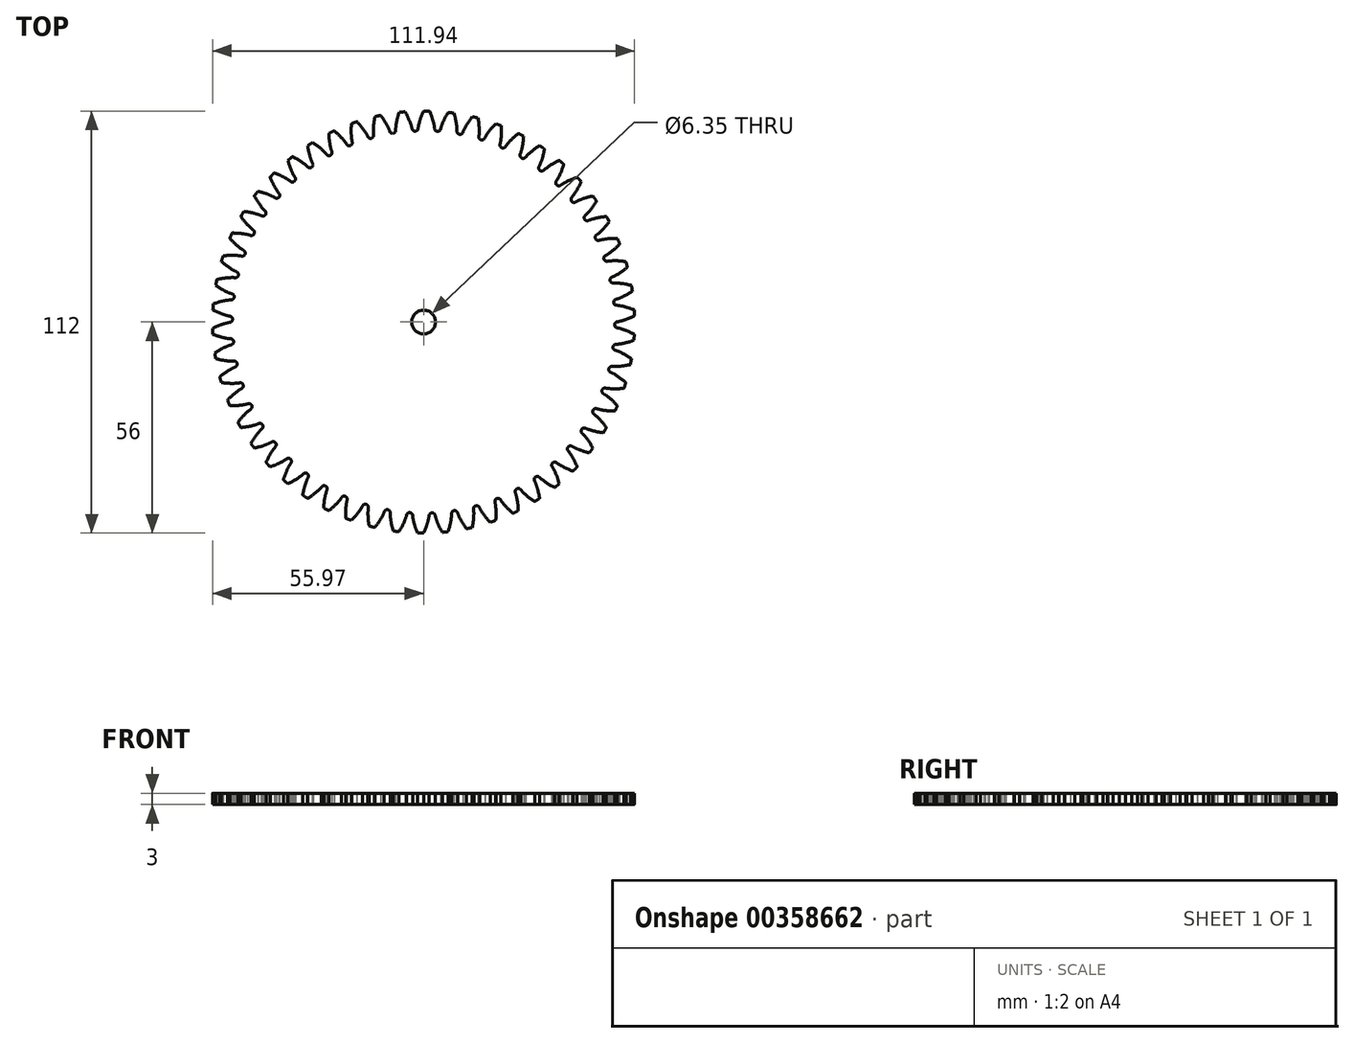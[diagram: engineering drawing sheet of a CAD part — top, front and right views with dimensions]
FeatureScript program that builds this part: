
annotation { "Feature Type Name" : "Feature", "Feature Type Description" : "" }
export const myFeature = defineFeature(function(context is Context, id is Id, definition is map)
    precondition{}
    {
        {
            assignVariable(context, id + "F0", {"name" : "T", "anyValue" : 54});
        }
        {
            var Q0;
            Q0=qCreatedBy(makeId("Top.planeOp"),FACE);
            var sketch = newSketch(context, id + "F1", { "sketchPlane" : qUnion([Q0])});
            skCircle(sketch, "E0", {"center": v(0, 0) * mm, "radius": 56 * mm});
            skCircle(sketch, "E1", {"center": v(0, 0) * mm, "radius": 54 * mm, "construction": true});
            skCircle(sketch, "E2", {"center": v(0, 0) * mm, "radius": 50.74 * mm, "construction": true});
            skCircle(sketch, "E3", {"center": v(0, 0) * mm, "radius": 51.5 * mm});
            skLineSegment(sketch, "E4", {"start": v(0, 0) * mm, "end": v(50.74, 0) * mm});
            skFitSpline(sketch, "E5", {"points": [v(50.74, 0) * mm, v(50.89, 0) * mm, v(51.3, 0.06) * mm, v(52, 0.2) * mm, v(52.97, 0.45) * mm, v(54.17, 0.87) * mm, v(55.6, 1.5) * mm, v(57.23, 2.36) * mm, v(59.03, 3.5) * mm, v(60.98, 4.93) * mm, v(63.02, 6.7) * mm], "startDerivative": vector(12.72, 0.63) * mm, "endDerivative": vector(42.04, 36.24) * mm});
            skLineSegment(sketch, "E6", {"start": v(0, 0) * mm, "end": v(56, -0.8) * mm, "construction": true});
            skLineSegment(sketch, "E7", {"start": v(0, 0) * mm, "end": v(54, 0.8) * mm, "construction": true});
            skFitSpline(sketch, "E8.MirrorCS", {"points": [v(50.72, -1.44) * mm, v(50.86, -1.45) * mm, v(51.29, -1.51) * mm, v(51.98, -1.67) * mm, v(52.93, -1.95) * mm, v(54.12, -2.4) * mm, v(55.54, -3.08) * mm, v(57.14, -3.99) * mm, v(58.91, -5.17) * mm, v(60.81, -6.66) * mm, v(62.8, -8.48) * mm], "startDerivative": vector(12.7, -1) * mm, "endDerivative": vector(41, -37.42) * mm});
            skLineSegment(sketch, "E9", {"start": v(0, 0) * mm, "end": v(50.72, -1.44) * mm});
            skSolve(sketch);
        }
        {
            var Q0;
            Q0=qCreatedBy(makeId("Top.planeOp"),FACE);
            var sketch = newSketch(context, id + "F2", { "sketchPlane" : qUnion([Q0])});
            skCircle(sketch, "E10", {"center": v(0, 0) * mm, "radius": 56 * mm});
            skSolve(sketch);
        }
        {
            var Q0;
            {var subQ0=sQuery(id+"F1.wireOp",EDGE,"E5");var subQ7=sQuery(id+"F1.wireOp",EDGE,"E0");var subQ8=makeQuery(id+"F1.imprint","INTERSECT",VERTEX,{"derivedFrom":[subQ7,subQ0]});Q0=makeQuery(id+"F1.imprint","IMPRINT",FACE,{"disambiguationData":[TD([[makeQuery(id+"F1.imprint","IMPRINT",EDGE,{"disambiguationData":[TD([[subQ8,1.0]])],"derivedFrom":subQ7}),1.0]])]});}
            extrude(context, id + "F3", {"entities" : qUnion([Q0]), "depth" : 6 * mm});
        }
        {
            var Q0;
            Q0=makeQuery(id+"F3.opExtrude","CAP_FACE",FACE,{"disambiguationData":[OSD([sQuery(id+"F1.wireOp",EDGE,"E0"),sQuery(id+"F1.wireOp",EDGE,"E3"),sQuery(id+"F1.wireOp",EDGE,"E4"),sQuery(id+"F1.wireOp",EDGE,"E5"),sQuery(id+"F1.wireOp",EDGE,"E8.MirrorCS"),sQuery(id+"F1.wireOp",EDGE,"E9")])],"isStart":true});
            var sketch = newSketch(context, id + "F4", { "sketchPlane" : qUnion([Q0])});
            skCircle(sketch, "E11", {"center": v(51.5, 0.73) * mm, "radius": 0.82 * mm});
            skSolve(sketch);
        }
        {
            var Q0;
            {var subQ1=makeQuery(id+"F3.opExtrude","CAP_EDGE",EDGE,{"disambiguationData":[OSD([sQuery(id+"F1.wireOp",EDGE,"E3")])],"isStart":true});Q0=makeQuery(id+"F4.imprint","IMPRINT",FACE,{"disambiguationData":[TD([[makeQuery(id+"F4.imprint","IMPRINT",EDGE,{"derivedFrom":subQ1}),-1.0]])]});}
            extrude(context, id + "F5", {"entities" : qUnion([Q0]), "operationType" : NewBodyOperationType.ADD, "oppositeDirection" : true, "depth" : 6 * mm});
        }
        {
            var Q0;
            Q0=makeQuery(id+"F2.imprint","IMPRINT",FACE,{"disambiguationData":[TD([[makeQuery(id+"F2.imprint","IMPRINT",EDGE,{"derivedFrom":sQuery(id+"F2.wireOp",EDGE,"E10")}),1.0]])]});
            extrude(context, id + "F6", {"entities" : qUnion([Q0]), "depth" : 3 * mm, "offsetDistance" : 25 * mm});
        }
        {
            var Q0;
            Q0=makeQuery(id+"F3.opExtrude","SWEPT_BODY",BODY,{"disambiguationData":[OSD([sQuery(id+"F1.wireOp",EDGE,"E0"),sQuery(id+"F1.wireOp",EDGE,"E3"),sQuery(id+"F1.wireOp",EDGE,"E4"),sQuery(id+"F1.wireOp",EDGE,"E5"),sQuery(id+"F1.wireOp",EDGE,"E8.MirrorCS"),sQuery(id+"F1.wireOp",EDGE,"E9")])]});
            var Q1;
            Q1=makeQuery(id+"F6.opExtrude","CAP_EDGE",EDGE,{"disambiguationData":[OSD([sQuery(id+"F2.wireOp",EDGE,"E10")])],"isStart":false});
            circularPattern(context, id + "F7", {"entities" : qUnion([Q0]), "axis" : qUnion([Q1]), "angle" : 360 * degree, "instanceCount" : getVariable(context, 'T'), "equalSpace" : true});
        }
        {
            var Q0;
            Q0=makeQuery(id+"F7.opPattern","COPY",BODY,{"derivedFrom":makeQuery(id+"F3.opExtrude","SWEPT_BODY",BODY,{"disambiguationData":[OSD([sQuery(id+"F1.wireOp",EDGE,"E0"),sQuery(id+"F1.wireOp",EDGE,"E3"),sQuery(id+"F1.wireOp",EDGE,"E4"),sQuery(id+"F1.wireOp",EDGE,"E5"),sQuery(id+"F1.wireOp",EDGE,"E8.MirrorCS"),sQuery(id+"F1.wireOp",EDGE,"E9")])]}),"instanceName":"5"});
            var Q1;
            Q1=makeQuery(id+"F7.opPattern","COPY",BODY,{"derivedFrom":makeQuery(id+"F3.opExtrude","SWEPT_BODY",BODY,{"disambiguationData":[OSD([sQuery(id+"F1.wireOp",EDGE,"E0"),sQuery(id+"F1.wireOp",EDGE,"E3"),sQuery(id+"F1.wireOp",EDGE,"E4"),sQuery(id+"F1.wireOp",EDGE,"E5"),sQuery(id+"F1.wireOp",EDGE,"E8.MirrorCS"),sQuery(id+"F1.wireOp",EDGE,"E9")])]}),"instanceName":"6"});
            var Q2;
            Q2=makeQuery(id+"F7.opPattern","COPY",BODY,{"derivedFrom":makeQuery(id+"F3.opExtrude","SWEPT_BODY",BODY,{"disambiguationData":[OSD([sQuery(id+"F1.wireOp",EDGE,"E0"),sQuery(id+"F1.wireOp",EDGE,"E3"),sQuery(id+"F1.wireOp",EDGE,"E4"),sQuery(id+"F1.wireOp",EDGE,"E5"),sQuery(id+"F1.wireOp",EDGE,"E8.MirrorCS"),sQuery(id+"F1.wireOp",EDGE,"E9")])]}),"instanceName":"7"});
            var Q3;
            Q3=makeQuery(id+"F7.opPattern","COPY",BODY,{"derivedFrom":makeQuery(id+"F3.opExtrude","SWEPT_BODY",BODY,{"disambiguationData":[OSD([sQuery(id+"F1.wireOp",EDGE,"E0"),sQuery(id+"F1.wireOp",EDGE,"E3"),sQuery(id+"F1.wireOp",EDGE,"E4"),sQuery(id+"F1.wireOp",EDGE,"E5"),sQuery(id+"F1.wireOp",EDGE,"E8.MirrorCS"),sQuery(id+"F1.wireOp",EDGE,"E9")])]}),"instanceName":"8"});
            var Q4;
            Q4=makeQuery(id+"F7.opPattern","COPY",BODY,{"derivedFrom":makeQuery(id+"F3.opExtrude","SWEPT_BODY",BODY,{"disambiguationData":[OSD([sQuery(id+"F1.wireOp",EDGE,"E0"),sQuery(id+"F1.wireOp",EDGE,"E3"),sQuery(id+"F1.wireOp",EDGE,"E4"),sQuery(id+"F1.wireOp",EDGE,"E5"),sQuery(id+"F1.wireOp",EDGE,"E8.MirrorCS"),sQuery(id+"F1.wireOp",EDGE,"E9")])]}),"instanceName":"9"});
            var Q5;
            Q5=makeQuery(id+"F7.opPattern","COPY",BODY,{"derivedFrom":makeQuery(id+"F3.opExtrude","SWEPT_BODY",BODY,{"disambiguationData":[OSD([sQuery(id+"F1.wireOp",EDGE,"E0"),sQuery(id+"F1.wireOp",EDGE,"E3"),sQuery(id+"F1.wireOp",EDGE,"E4"),sQuery(id+"F1.wireOp",EDGE,"E5"),sQuery(id+"F1.wireOp",EDGE,"E8.MirrorCS"),sQuery(id+"F1.wireOp",EDGE,"E9")])]}),"instanceName":"10"});
            var Q6;
            Q6=makeQuery(id+"F7.opPattern","COPY",BODY,{"derivedFrom":makeQuery(id+"F3.opExtrude","SWEPT_BODY",BODY,{"disambiguationData":[OSD([sQuery(id+"F1.wireOp",EDGE,"E0"),sQuery(id+"F1.wireOp",EDGE,"E3"),sQuery(id+"F1.wireOp",EDGE,"E4"),sQuery(id+"F1.wireOp",EDGE,"E5"),sQuery(id+"F1.wireOp",EDGE,"E8.MirrorCS"),sQuery(id+"F1.wireOp",EDGE,"E9")])]}),"instanceName":"11"});
            var Q7;
            Q7=makeQuery(id+"F7.opPattern","COPY",BODY,{"derivedFrom":makeQuery(id+"F3.opExtrude","SWEPT_BODY",BODY,{"disambiguationData":[OSD([sQuery(id+"F1.wireOp",EDGE,"E0"),sQuery(id+"F1.wireOp",EDGE,"E3"),sQuery(id+"F1.wireOp",EDGE,"E4"),sQuery(id+"F1.wireOp",EDGE,"E5"),sQuery(id+"F1.wireOp",EDGE,"E8.MirrorCS"),sQuery(id+"F1.wireOp",EDGE,"E9")])]}),"instanceName":"12"});
            var Q8;
            Q8=makeQuery(id+"F7.opPattern","COPY",BODY,{"derivedFrom":makeQuery(id+"F3.opExtrude","SWEPT_BODY",BODY,{"disambiguationData":[OSD([sQuery(id+"F1.wireOp",EDGE,"E0"),sQuery(id+"F1.wireOp",EDGE,"E3"),sQuery(id+"F1.wireOp",EDGE,"E4"),sQuery(id+"F1.wireOp",EDGE,"E5"),sQuery(id+"F1.wireOp",EDGE,"E8.MirrorCS"),sQuery(id+"F1.wireOp",EDGE,"E9")])]}),"instanceName":"13"});
            var Q9;
            Q9=makeQuery(id+"F7.opPattern","COPY",BODY,{"derivedFrom":makeQuery(id+"F3.opExtrude","SWEPT_BODY",BODY,{"disambiguationData":[OSD([sQuery(id+"F1.wireOp",EDGE,"E0"),sQuery(id+"F1.wireOp",EDGE,"E3"),sQuery(id+"F1.wireOp",EDGE,"E4"),sQuery(id+"F1.wireOp",EDGE,"E5"),sQuery(id+"F1.wireOp",EDGE,"E8.MirrorCS"),sQuery(id+"F1.wireOp",EDGE,"E9")])]}),"instanceName":"14"});
            var Q10;
            Q10=makeQuery(id+"F7.opPattern","COPY",BODY,{"derivedFrom":makeQuery(id+"F3.opExtrude","SWEPT_BODY",BODY,{"disambiguationData":[OSD([sQuery(id+"F1.wireOp",EDGE,"E0"),sQuery(id+"F1.wireOp",EDGE,"E3"),sQuery(id+"F1.wireOp",EDGE,"E4"),sQuery(id+"F1.wireOp",EDGE,"E5"),sQuery(id+"F1.wireOp",EDGE,"E8.MirrorCS"),sQuery(id+"F1.wireOp",EDGE,"E9")])]}),"instanceName":"15"});
            var Q11;
            Q11=makeQuery(id+"F7.opPattern","COPY",BODY,{"derivedFrom":makeQuery(id+"F3.opExtrude","SWEPT_BODY",BODY,{"disambiguationData":[OSD([sQuery(id+"F1.wireOp",EDGE,"E0"),sQuery(id+"F1.wireOp",EDGE,"E3"),sQuery(id+"F1.wireOp",EDGE,"E4"),sQuery(id+"F1.wireOp",EDGE,"E5"),sQuery(id+"F1.wireOp",EDGE,"E8.MirrorCS"),sQuery(id+"F1.wireOp",EDGE,"E9")])]}),"instanceName":"16"});
            var Q12;
            Q12=makeQuery(id+"F7.opPattern","COPY",BODY,{"derivedFrom":makeQuery(id+"F3.opExtrude","SWEPT_BODY",BODY,{"disambiguationData":[OSD([sQuery(id+"F1.wireOp",EDGE,"E0"),sQuery(id+"F1.wireOp",EDGE,"E3"),sQuery(id+"F1.wireOp",EDGE,"E4"),sQuery(id+"F1.wireOp",EDGE,"E5"),sQuery(id+"F1.wireOp",EDGE,"E8.MirrorCS"),sQuery(id+"F1.wireOp",EDGE,"E9")])]}),"instanceName":"17"});
            var Q13;
            Q13=makeQuery(id+"F7.opPattern","COPY",BODY,{"derivedFrom":makeQuery(id+"F3.opExtrude","SWEPT_BODY",BODY,{"disambiguationData":[OSD([sQuery(id+"F1.wireOp",EDGE,"E0"),sQuery(id+"F1.wireOp",EDGE,"E3"),sQuery(id+"F1.wireOp",EDGE,"E4"),sQuery(id+"F1.wireOp",EDGE,"E5"),sQuery(id+"F1.wireOp",EDGE,"E8.MirrorCS"),sQuery(id+"F1.wireOp",EDGE,"E9")])]}),"instanceName":"18"});
            var Q14;
            Q14=makeQuery(id+"F7.opPattern","COPY",BODY,{"derivedFrom":makeQuery(id+"F3.opExtrude","SWEPT_BODY",BODY,{"disambiguationData":[OSD([sQuery(id+"F1.wireOp",EDGE,"E0"),sQuery(id+"F1.wireOp",EDGE,"E3"),sQuery(id+"F1.wireOp",EDGE,"E4"),sQuery(id+"F1.wireOp",EDGE,"E5"),sQuery(id+"F1.wireOp",EDGE,"E8.MirrorCS"),sQuery(id+"F1.wireOp",EDGE,"E9")])]}),"instanceName":"19"});
            var Q15;
            Q15=makeQuery(id+"F7.opPattern","COPY",BODY,{"derivedFrom":makeQuery(id+"F3.opExtrude","SWEPT_BODY",BODY,{"disambiguationData":[OSD([sQuery(id+"F1.wireOp",EDGE,"E0"),sQuery(id+"F1.wireOp",EDGE,"E3"),sQuery(id+"F1.wireOp",EDGE,"E4"),sQuery(id+"F1.wireOp",EDGE,"E5"),sQuery(id+"F1.wireOp",EDGE,"E8.MirrorCS"),sQuery(id+"F1.wireOp",EDGE,"E9")])]}),"instanceName":"20"});
            var Q16;
            Q16=makeQuery(id+"F7.opPattern","COPY",BODY,{"derivedFrom":makeQuery(id+"F3.opExtrude","SWEPT_BODY",BODY,{"disambiguationData":[OSD([sQuery(id+"F1.wireOp",EDGE,"E0"),sQuery(id+"F1.wireOp",EDGE,"E3"),sQuery(id+"F1.wireOp",EDGE,"E4"),sQuery(id+"F1.wireOp",EDGE,"E5"),sQuery(id+"F1.wireOp",EDGE,"E8.MirrorCS"),sQuery(id+"F1.wireOp",EDGE,"E9")])]}),"instanceName":"21"});
            var Q17;
            Q17=makeQuery(id+"F7.opPattern","COPY",BODY,{"derivedFrom":makeQuery(id+"F3.opExtrude","SWEPT_BODY",BODY,{"disambiguationData":[OSD([sQuery(id+"F1.wireOp",EDGE,"E0"),sQuery(id+"F1.wireOp",EDGE,"E3"),sQuery(id+"F1.wireOp",EDGE,"E4"),sQuery(id+"F1.wireOp",EDGE,"E5"),sQuery(id+"F1.wireOp",EDGE,"E8.MirrorCS"),sQuery(id+"F1.wireOp",EDGE,"E9")])]}),"instanceName":"22"});
            var Q18;
            Q18=makeQuery(id+"F7.opPattern","COPY",BODY,{"derivedFrom":makeQuery(id+"F3.opExtrude","SWEPT_BODY",BODY,{"disambiguationData":[OSD([sQuery(id+"F1.wireOp",EDGE,"E0"),sQuery(id+"F1.wireOp",EDGE,"E3"),sQuery(id+"F1.wireOp",EDGE,"E4"),sQuery(id+"F1.wireOp",EDGE,"E5"),sQuery(id+"F1.wireOp",EDGE,"E8.MirrorCS"),sQuery(id+"F1.wireOp",EDGE,"E9")])]}),"instanceName":"23"});
            var Q19;
            Q19=makeQuery(id+"F7.opPattern","COPY",BODY,{"derivedFrom":makeQuery(id+"F3.opExtrude","SWEPT_BODY",BODY,{"disambiguationData":[OSD([sQuery(id+"F1.wireOp",EDGE,"E0"),sQuery(id+"F1.wireOp",EDGE,"E3"),sQuery(id+"F1.wireOp",EDGE,"E4"),sQuery(id+"F1.wireOp",EDGE,"E5"),sQuery(id+"F1.wireOp",EDGE,"E8.MirrorCS"),sQuery(id+"F1.wireOp",EDGE,"E9")])]}),"instanceName":"24"});
            var Q20;
            Q20=makeQuery(id+"F7.opPattern","COPY",BODY,{"derivedFrom":makeQuery(id+"F3.opExtrude","SWEPT_BODY",BODY,{"disambiguationData":[OSD([sQuery(id+"F1.wireOp",EDGE,"E0"),sQuery(id+"F1.wireOp",EDGE,"E3"),sQuery(id+"F1.wireOp",EDGE,"E4"),sQuery(id+"F1.wireOp",EDGE,"E5"),sQuery(id+"F1.wireOp",EDGE,"E8.MirrorCS"),sQuery(id+"F1.wireOp",EDGE,"E9")])]}),"instanceName":"25"});
            var Q21;
            Q21=makeQuery(id+"F7.opPattern","COPY",BODY,{"derivedFrom":makeQuery(id+"F3.opExtrude","SWEPT_BODY",BODY,{"disambiguationData":[OSD([sQuery(id+"F1.wireOp",EDGE,"E0"),sQuery(id+"F1.wireOp",EDGE,"E3"),sQuery(id+"F1.wireOp",EDGE,"E4"),sQuery(id+"F1.wireOp",EDGE,"E5"),sQuery(id+"F1.wireOp",EDGE,"E8.MirrorCS"),sQuery(id+"F1.wireOp",EDGE,"E9")])]}),"instanceName":"26"});
            var Q22;
            Q22=makeQuery(id+"F7.opPattern","COPY",BODY,{"derivedFrom":makeQuery(id+"F3.opExtrude","SWEPT_BODY",BODY,{"disambiguationData":[OSD([sQuery(id+"F1.wireOp",EDGE,"E0"),sQuery(id+"F1.wireOp",EDGE,"E3"),sQuery(id+"F1.wireOp",EDGE,"E4"),sQuery(id+"F1.wireOp",EDGE,"E5"),sQuery(id+"F1.wireOp",EDGE,"E8.MirrorCS"),sQuery(id+"F1.wireOp",EDGE,"E9")])]}),"instanceName":"27"});
            var Q23;
            Q23=makeQuery(id+"F7.opPattern","COPY",BODY,{"derivedFrom":makeQuery(id+"F3.opExtrude","SWEPT_BODY",BODY,{"disambiguationData":[OSD([sQuery(id+"F1.wireOp",EDGE,"E0"),sQuery(id+"F1.wireOp",EDGE,"E3"),sQuery(id+"F1.wireOp",EDGE,"E4"),sQuery(id+"F1.wireOp",EDGE,"E5"),sQuery(id+"F1.wireOp",EDGE,"E8.MirrorCS"),sQuery(id+"F1.wireOp",EDGE,"E9")])]}),"instanceName":"28"});
            var Q24;
            Q24=makeQuery(id+"F7.opPattern","COPY",BODY,{"derivedFrom":makeQuery(id+"F3.opExtrude","SWEPT_BODY",BODY,{"disambiguationData":[OSD([sQuery(id+"F1.wireOp",EDGE,"E0"),sQuery(id+"F1.wireOp",EDGE,"E3"),sQuery(id+"F1.wireOp",EDGE,"E4"),sQuery(id+"F1.wireOp",EDGE,"E5"),sQuery(id+"F1.wireOp",EDGE,"E8.MirrorCS"),sQuery(id+"F1.wireOp",EDGE,"E9")])]}),"instanceName":"29"});
            var Q25;
            Q25=makeQuery(id+"F3.opExtrude","SWEPT_BODY",BODY,{"disambiguationData":[OSD([sQuery(id+"F1.wireOp",EDGE,"E0"),sQuery(id+"F1.wireOp",EDGE,"E3"),sQuery(id+"F1.wireOp",EDGE,"E4"),sQuery(id+"F1.wireOp",EDGE,"E5"),sQuery(id+"F1.wireOp",EDGE,"E8.MirrorCS"),sQuery(id+"F1.wireOp",EDGE,"E9")])]});
            var Q26;
            Q26=makeQuery(id+"F7.opPattern","COPY",BODY,{"derivedFrom":makeQuery(id+"F3.opExtrude","SWEPT_BODY",BODY,{"disambiguationData":[OSD([sQuery(id+"F1.wireOp",EDGE,"E0"),sQuery(id+"F1.wireOp",EDGE,"E3"),sQuery(id+"F1.wireOp",EDGE,"E4"),sQuery(id+"F1.wireOp",EDGE,"E5"),sQuery(id+"F1.wireOp",EDGE,"E8.MirrorCS"),sQuery(id+"F1.wireOp",EDGE,"E9")])]}),"instanceName":"1"});
            var Q27;
            Q27=makeQuery(id+"F7.opPattern","COPY",BODY,{"derivedFrom":makeQuery(id+"F3.opExtrude","SWEPT_BODY",BODY,{"disambiguationData":[OSD([sQuery(id+"F1.wireOp",EDGE,"E0"),sQuery(id+"F1.wireOp",EDGE,"E3"),sQuery(id+"F1.wireOp",EDGE,"E4"),sQuery(id+"F1.wireOp",EDGE,"E5"),sQuery(id+"F1.wireOp",EDGE,"E8.MirrorCS"),sQuery(id+"F1.wireOp",EDGE,"E9")])]}),"instanceName":"2"});
            var Q28;
            Q28=makeQuery(id+"F7.opPattern","COPY",BODY,{"derivedFrom":makeQuery(id+"F3.opExtrude","SWEPT_BODY",BODY,{"disambiguationData":[OSD([sQuery(id+"F1.wireOp",EDGE,"E0"),sQuery(id+"F1.wireOp",EDGE,"E3"),sQuery(id+"F1.wireOp",EDGE,"E4"),sQuery(id+"F1.wireOp",EDGE,"E5"),sQuery(id+"F1.wireOp",EDGE,"E8.MirrorCS"),sQuery(id+"F1.wireOp",EDGE,"E9")])]}),"instanceName":"3"});
            var Q29;
            Q29=makeQuery(id+"F7.opPattern","COPY",BODY,{"derivedFrom":makeQuery(id+"F3.opExtrude","SWEPT_BODY",BODY,{"disambiguationData":[OSD([sQuery(id+"F1.wireOp",EDGE,"E0"),sQuery(id+"F1.wireOp",EDGE,"E3"),sQuery(id+"F1.wireOp",EDGE,"E4"),sQuery(id+"F1.wireOp",EDGE,"E5"),sQuery(id+"F1.wireOp",EDGE,"E8.MirrorCS"),sQuery(id+"F1.wireOp",EDGE,"E9")])]}),"instanceName":"4"});
            var Q30;
            Q30=makeQuery(id+"F7.opPattern","COPY",BODY,{"derivedFrom":makeQuery(id+"F3.opExtrude","SWEPT_BODY",BODY,{"disambiguationData":[OSD([sQuery(id+"F1.wireOp",EDGE,"E0"),sQuery(id+"F1.wireOp",EDGE,"E3"),sQuery(id+"F1.wireOp",EDGE,"E5"),sQuery(id+"F1.wireOp",EDGE,"E8.MirrorCS")])]}),"instanceName":"30"});
            var Q31;
            Q31=makeQuery(id+"F7.opPattern","COPY",BODY,{"derivedFrom":makeQuery(id+"F3.opExtrude","SWEPT_BODY",BODY,{"disambiguationData":[OSD([sQuery(id+"F1.wireOp",EDGE,"E0"),sQuery(id+"F1.wireOp",EDGE,"E3"),sQuery(id+"F1.wireOp",EDGE,"E5"),sQuery(id+"F1.wireOp",EDGE,"E8.MirrorCS")])]}),"instanceName":"31"});
            var Q32;
            Q32=makeQuery(id+"F7.opPattern","COPY",BODY,{"derivedFrom":makeQuery(id+"F3.opExtrude","SWEPT_BODY",BODY,{"disambiguationData":[OSD([sQuery(id+"F1.wireOp",EDGE,"E0"),sQuery(id+"F1.wireOp",EDGE,"E3"),sQuery(id+"F1.wireOp",EDGE,"E5"),sQuery(id+"F1.wireOp",EDGE,"E8.MirrorCS")])]}),"instanceName":"32"});
            var Q33;
            Q33=makeQuery(id+"F7.opPattern","COPY",BODY,{"derivedFrom":makeQuery(id+"F3.opExtrude","SWEPT_BODY",BODY,{"disambiguationData":[OSD([sQuery(id+"F1.wireOp",EDGE,"E0"),sQuery(id+"F1.wireOp",EDGE,"E3"),sQuery(id+"F1.wireOp",EDGE,"E5"),sQuery(id+"F1.wireOp",EDGE,"E8.MirrorCS")])]}),"instanceName":"33"});
            var Q34;
            Q34=makeQuery(id+"F7.opPattern","COPY",BODY,{"derivedFrom":makeQuery(id+"F3.opExtrude","SWEPT_BODY",BODY,{"disambiguationData":[OSD([sQuery(id+"F1.wireOp",EDGE,"E0"),sQuery(id+"F1.wireOp",EDGE,"E3"),sQuery(id+"F1.wireOp",EDGE,"E5"),sQuery(id+"F1.wireOp",EDGE,"E8.MirrorCS")])]}),"instanceName":"34"});
            var Q35;
            Q35=makeQuery(id+"F7.opPattern","COPY",BODY,{"derivedFrom":makeQuery(id+"F3.opExtrude","SWEPT_BODY",BODY,{"disambiguationData":[OSD([sQuery(id+"F1.wireOp",EDGE,"E0"),sQuery(id+"F1.wireOp",EDGE,"E3"),sQuery(id+"F1.wireOp",EDGE,"E5"),sQuery(id+"F1.wireOp",EDGE,"E8.MirrorCS")])]}),"instanceName":"35"});
            var Q36;
            Q36=makeQuery(id+"F7.opPattern","COPY",BODY,{"derivedFrom":makeQuery(id+"F3.opExtrude","SWEPT_BODY",BODY,{"disambiguationData":[OSD([sQuery(id+"F1.wireOp",EDGE,"E0"),sQuery(id+"F1.wireOp",EDGE,"E3"),sQuery(id+"F1.wireOp",EDGE,"E5"),sQuery(id+"F1.wireOp",EDGE,"E8.MirrorCS")])]}),"instanceName":"36"});
            var Q37;
            Q37=makeQuery(id+"F7.opPattern","COPY",BODY,{"derivedFrom":makeQuery(id+"F3.opExtrude","SWEPT_BODY",BODY,{"disambiguationData":[OSD([sQuery(id+"F1.wireOp",EDGE,"E0"),sQuery(id+"F1.wireOp",EDGE,"E3"),sQuery(id+"F1.wireOp",EDGE,"E5"),sQuery(id+"F1.wireOp",EDGE,"E8.MirrorCS")])]}),"instanceName":"37"});
            var Q38;
            Q38=makeQuery(id+"F7.opPattern","COPY",BODY,{"derivedFrom":makeQuery(id+"F3.opExtrude","SWEPT_BODY",BODY,{"disambiguationData":[OSD([sQuery(id+"F1.wireOp",EDGE,"E0"),sQuery(id+"F1.wireOp",EDGE,"E3"),sQuery(id+"F1.wireOp",EDGE,"E5"),sQuery(id+"F1.wireOp",EDGE,"E8.MirrorCS")])]}),"instanceName":"38"});
            var Q39;
            Q39=makeQuery(id+"F7.opPattern","COPY",BODY,{"derivedFrom":makeQuery(id+"F3.opExtrude","SWEPT_BODY",BODY,{"disambiguationData":[OSD([sQuery(id+"F1.wireOp",EDGE,"E0"),sQuery(id+"F1.wireOp",EDGE,"E3"),sQuery(id+"F1.wireOp",EDGE,"E5"),sQuery(id+"F1.wireOp",EDGE,"E8.MirrorCS")])]}),"instanceName":"39"});
            var Q40;
            Q40=makeQuery(id+"F7.opPattern","COPY",BODY,{"derivedFrom":makeQuery(id+"F3.opExtrude","SWEPT_BODY",BODY,{"disambiguationData":[OSD([sQuery(id+"F1.wireOp",EDGE,"E0"),sQuery(id+"F1.wireOp",EDGE,"E3"),sQuery(id+"F1.wireOp",EDGE,"E5"),sQuery(id+"F1.wireOp",EDGE,"E8.MirrorCS")])]}),"instanceName":"40"});
            var Q41;
            Q41=makeQuery(id+"F7.opPattern","COPY",BODY,{"derivedFrom":makeQuery(id+"F3.opExtrude","SWEPT_BODY",BODY,{"disambiguationData":[OSD([sQuery(id+"F1.wireOp",EDGE,"E0"),sQuery(id+"F1.wireOp",EDGE,"E3"),sQuery(id+"F1.wireOp",EDGE,"E5"),sQuery(id+"F1.wireOp",EDGE,"E8.MirrorCS")])]}),"instanceName":"41"});
            var Q42;
            Q42=makeQuery(id+"F7.opPattern","COPY",BODY,{"derivedFrom":makeQuery(id+"F3.opExtrude","SWEPT_BODY",BODY,{"disambiguationData":[OSD([sQuery(id+"F1.wireOp",EDGE,"E0"),sQuery(id+"F1.wireOp",EDGE,"E3"),sQuery(id+"F1.wireOp",EDGE,"E5"),sQuery(id+"F1.wireOp",EDGE,"E8.MirrorCS")])]}),"instanceName":"42"});
            var Q43;
            Q43=makeQuery(id+"F7.opPattern","COPY",BODY,{"derivedFrom":makeQuery(id+"F3.opExtrude","SWEPT_BODY",BODY,{"disambiguationData":[OSD([sQuery(id+"F1.wireOp",EDGE,"E0"),sQuery(id+"F1.wireOp",EDGE,"E3"),sQuery(id+"F1.wireOp",EDGE,"E5"),sQuery(id+"F1.wireOp",EDGE,"E8.MirrorCS")])]}),"instanceName":"43"});
            var Q44;
            Q44=makeQuery(id+"F7.opPattern","COPY",BODY,{"derivedFrom":makeQuery(id+"F3.opExtrude","SWEPT_BODY",BODY,{"disambiguationData":[OSD([sQuery(id+"F1.wireOp",EDGE,"E0"),sQuery(id+"F1.wireOp",EDGE,"E3"),sQuery(id+"F1.wireOp",EDGE,"E5"),sQuery(id+"F1.wireOp",EDGE,"E8.MirrorCS")])]}),"instanceName":"44"});
            var Q45;
            Q45=makeQuery(id+"F7.opPattern","COPY",BODY,{"derivedFrom":makeQuery(id+"F3.opExtrude","SWEPT_BODY",BODY,{"disambiguationData":[OSD([sQuery(id+"F1.wireOp",EDGE,"E0"),sQuery(id+"F1.wireOp",EDGE,"E3"),sQuery(id+"F1.wireOp",EDGE,"E5"),sQuery(id+"F1.wireOp",EDGE,"E8.MirrorCS")])]}),"instanceName":"45"});
            var Q46;
            Q46=makeQuery(id+"F7.opPattern","COPY",BODY,{"derivedFrom":makeQuery(id+"F3.opExtrude","SWEPT_BODY",BODY,{"disambiguationData":[OSD([sQuery(id+"F1.wireOp",EDGE,"E0"),sQuery(id+"F1.wireOp",EDGE,"E3"),sQuery(id+"F1.wireOp",EDGE,"E5"),sQuery(id+"F1.wireOp",EDGE,"E8.MirrorCS")])]}),"instanceName":"46"});
            var Q47;
            Q47=makeQuery(id+"F7.opPattern","COPY",BODY,{"derivedFrom":makeQuery(id+"F3.opExtrude","SWEPT_BODY",BODY,{"disambiguationData":[OSD([sQuery(id+"F1.wireOp",EDGE,"E0"),sQuery(id+"F1.wireOp",EDGE,"E3"),sQuery(id+"F1.wireOp",EDGE,"E5"),sQuery(id+"F1.wireOp",EDGE,"E8.MirrorCS")])]}),"instanceName":"47"});
            var Q48;
            Q48=makeQuery(id+"F7.opPattern","COPY",BODY,{"derivedFrom":makeQuery(id+"F3.opExtrude","SWEPT_BODY",BODY,{"disambiguationData":[OSD([sQuery(id+"F1.wireOp",EDGE,"E0"),sQuery(id+"F1.wireOp",EDGE,"E3"),sQuery(id+"F1.wireOp",EDGE,"E5"),sQuery(id+"F1.wireOp",EDGE,"E8.MirrorCS")])]}),"instanceName":"48"});
            var Q49;
            Q49=makeQuery(id+"F7.opPattern","COPY",BODY,{"derivedFrom":makeQuery(id+"F3.opExtrude","SWEPT_BODY",BODY,{"disambiguationData":[OSD([sQuery(id+"F1.wireOp",EDGE,"E0"),sQuery(id+"F1.wireOp",EDGE,"E3"),sQuery(id+"F1.wireOp",EDGE,"E5"),sQuery(id+"F1.wireOp",EDGE,"E8.MirrorCS")])]}),"instanceName":"49"});
            var Q50;
            Q50=makeQuery(id+"F7.opPattern","COPY",BODY,{"derivedFrom":makeQuery(id+"F3.opExtrude","SWEPT_BODY",BODY,{"disambiguationData":[OSD([sQuery(id+"F1.wireOp",EDGE,"E0"),sQuery(id+"F1.wireOp",EDGE,"E3"),sQuery(id+"F1.wireOp",EDGE,"E5"),sQuery(id+"F1.wireOp",EDGE,"E8.MirrorCS")])]}),"instanceName":"50"});
            var Q51;
            Q51=makeQuery(id+"F7.opPattern","COPY",BODY,{"derivedFrom":makeQuery(id+"F3.opExtrude","SWEPT_BODY",BODY,{"disambiguationData":[OSD([sQuery(id+"F1.wireOp",EDGE,"E0"),sQuery(id+"F1.wireOp",EDGE,"E3"),sQuery(id+"F1.wireOp",EDGE,"E5"),sQuery(id+"F1.wireOp",EDGE,"E8.MirrorCS")])]}),"instanceName":"51"});
            var Q52;
            Q52=makeQuery(id+"F7.opPattern","COPY",BODY,{"derivedFrom":makeQuery(id+"F3.opExtrude","SWEPT_BODY",BODY,{"disambiguationData":[OSD([sQuery(id+"F1.wireOp",EDGE,"E0"),sQuery(id+"F1.wireOp",EDGE,"E3"),sQuery(id+"F1.wireOp",EDGE,"E5"),sQuery(id+"F1.wireOp",EDGE,"E8.MirrorCS")])]}),"instanceName":"52"});
            var Q53;
            Q53=makeQuery(id+"F7.opPattern","COPY",BODY,{"derivedFrom":makeQuery(id+"F3.opExtrude","SWEPT_BODY",BODY,{"disambiguationData":[OSD([sQuery(id+"F1.wireOp",EDGE,"E0"),sQuery(id+"F1.wireOp",EDGE,"E3"),sQuery(id+"F1.wireOp",EDGE,"E5"),sQuery(id+"F1.wireOp",EDGE,"E8.MirrorCS")])]}),"instanceName":"53"});
            var Q54;
            Q54=makeQuery(id+"F7.opPattern","COPY",BODY,{"derivedFrom":makeQuery(id+"F3.opExtrude","SWEPT_BODY",BODY,{"disambiguationData":[OSD([sQuery(id+"F1.wireOp",EDGE,"E0"),sQuery(id+"F1.wireOp",EDGE,"E3"),sQuery(id+"F1.wireOp",EDGE,"E5"),sQuery(id+"F1.wireOp",EDGE,"E8.MirrorCS")])]}),"instanceName":"54"});
            var Q55;
            Q55=makeQuery(id+"F7.opPattern","COPY",BODY,{"derivedFrom":makeQuery(id+"F3.opExtrude","SWEPT_BODY",BODY,{"disambiguationData":[OSD([sQuery(id+"F1.wireOp",EDGE,"E0"),sQuery(id+"F1.wireOp",EDGE,"E3"),sQuery(id+"F1.wireOp",EDGE,"E5"),sQuery(id+"F1.wireOp",EDGE,"E8.MirrorCS")])]}),"instanceName":"55"});
            var Q56;
            Q56=makeQuery(id+"F7.opPattern","COPY",BODY,{"derivedFrom":makeQuery(id+"F3.opExtrude","SWEPT_BODY",BODY,{"disambiguationData":[OSD([sQuery(id+"F1.wireOp",EDGE,"E0"),sQuery(id+"F1.wireOp",EDGE,"E3"),sQuery(id+"F1.wireOp",EDGE,"E5"),sQuery(id+"F1.wireOp",EDGE,"E8.MirrorCS")])]}),"instanceName":"56"});
            var Q57;
            Q57=makeQuery(id+"F7.opPattern","COPY",BODY,{"derivedFrom":makeQuery(id+"F3.opExtrude","SWEPT_BODY",BODY,{"disambiguationData":[OSD([sQuery(id+"F1.wireOp",EDGE,"E0"),sQuery(id+"F1.wireOp",EDGE,"E3"),sQuery(id+"F1.wireOp",EDGE,"E5"),sQuery(id+"F1.wireOp",EDGE,"E8.MirrorCS")])]}),"instanceName":"57"});
            var Q58;
            Q58=makeQuery(id+"F7.opPattern","COPY",BODY,{"derivedFrom":makeQuery(id+"F3.opExtrude","SWEPT_BODY",BODY,{"disambiguationData":[OSD([sQuery(id+"F1.wireOp",EDGE,"E0"),sQuery(id+"F1.wireOp",EDGE,"E3"),sQuery(id+"F1.wireOp",EDGE,"E5"),sQuery(id+"F1.wireOp",EDGE,"E8.MirrorCS")])]}),"instanceName":"58"});
            var Q59;
            Q59=makeQuery(id+"F7.opPattern","COPY",BODY,{"derivedFrom":makeQuery(id+"F3.opExtrude","SWEPT_BODY",BODY,{"disambiguationData":[OSD([sQuery(id+"F1.wireOp",EDGE,"E0"),sQuery(id+"F1.wireOp",EDGE,"E3"),sQuery(id+"F1.wireOp",EDGE,"E5"),sQuery(id+"F1.wireOp",EDGE,"E8.MirrorCS")])]}),"instanceName":"59"});
            var Q60;
            Q60=makeQuery(id+"F7.opPattern","COPY",BODY,{"derivedFrom":makeQuery(id+"F3.opExtrude","SWEPT_BODY",BODY,{"disambiguationData":[OSD([sQuery(id+"F1.wireOp",EDGE,"E0"),sQuery(id+"F1.wireOp",EDGE,"E3"),sQuery(id+"F1.wireOp",EDGE,"E5"),sQuery(id+"F1.wireOp",EDGE,"E8.MirrorCS")])]}),"instanceName":"60"});
            var Q61;
            Q61=makeQuery(id+"F7.opPattern","COPY",BODY,{"derivedFrom":makeQuery(id+"F3.opExtrude","SWEPT_BODY",BODY,{"disambiguationData":[OSD([sQuery(id+"F1.wireOp",EDGE,"E0"),sQuery(id+"F1.wireOp",EDGE,"E3"),sQuery(id+"F1.wireOp",EDGE,"E5"),sQuery(id+"F1.wireOp",EDGE,"E8.MirrorCS")])]}),"instanceName":"61"});
            var Q62;
            Q62=makeQuery(id+"F7.opPattern","COPY",BODY,{"derivedFrom":makeQuery(id+"F3.opExtrude","SWEPT_BODY",BODY,{"disambiguationData":[OSD([sQuery(id+"F1.wireOp",EDGE,"E0"),sQuery(id+"F1.wireOp",EDGE,"E3"),sQuery(id+"F1.wireOp",EDGE,"E5"),sQuery(id+"F1.wireOp",EDGE,"E8.MirrorCS")])]}),"instanceName":"62"});
            var Q63;
            Q63=makeQuery(id+"F7.opPattern","COPY",BODY,{"derivedFrom":makeQuery(id+"F3.opExtrude","SWEPT_BODY",BODY,{"disambiguationData":[OSD([sQuery(id+"F1.wireOp",EDGE,"E0"),sQuery(id+"F1.wireOp",EDGE,"E3"),sQuery(id+"F1.wireOp",EDGE,"E5"),sQuery(id+"F1.wireOp",EDGE,"E8.MirrorCS")])]}),"instanceName":"63"});
            var Q64;
            Q64=makeQuery(id+"F7.opPattern","COPY",BODY,{"derivedFrom":makeQuery(id+"F3.opExtrude","SWEPT_BODY",BODY,{"disambiguationData":[OSD([sQuery(id+"F1.wireOp",EDGE,"E0"),sQuery(id+"F1.wireOp",EDGE,"E3"),sQuery(id+"F1.wireOp",EDGE,"E5"),sQuery(id+"F1.wireOp",EDGE,"E8.MirrorCS")])]}),"instanceName":"64"});
            var Q65;
            Q65=makeQuery(id+"F7.opPattern","COPY",BODY,{"derivedFrom":makeQuery(id+"F3.opExtrude","SWEPT_BODY",BODY,{"disambiguationData":[OSD([sQuery(id+"F1.wireOp",EDGE,"E0"),sQuery(id+"F1.wireOp",EDGE,"E3"),sQuery(id+"F1.wireOp",EDGE,"E5"),sQuery(id+"F1.wireOp",EDGE,"E8.MirrorCS")])]}),"instanceName":"65"});
            var Q66;
            Q66=makeQuery(id+"F7.opPattern","COPY",BODY,{"derivedFrom":makeQuery(id+"F3.opExtrude","SWEPT_BODY",BODY,{"disambiguationData":[OSD([sQuery(id+"F1.wireOp",EDGE,"E0"),sQuery(id+"F1.wireOp",EDGE,"E3"),sQuery(id+"F1.wireOp",EDGE,"E5"),sQuery(id+"F1.wireOp",EDGE,"E8.MirrorCS")])]}),"instanceName":"66"});
            var Q67;
            Q67=makeQuery(id+"F7.opPattern","COPY",BODY,{"derivedFrom":makeQuery(id+"F3.opExtrude","SWEPT_BODY",BODY,{"disambiguationData":[OSD([sQuery(id+"F1.wireOp",EDGE,"E0"),sQuery(id+"F1.wireOp",EDGE,"E3"),sQuery(id+"F1.wireOp",EDGE,"E5"),sQuery(id+"F1.wireOp",EDGE,"E8.MirrorCS")])]}),"instanceName":"67"});
            var Q68;
            Q68=makeQuery(id+"F7.opPattern","COPY",BODY,{"derivedFrom":makeQuery(id+"F3.opExtrude","SWEPT_BODY",BODY,{"disambiguationData":[OSD([sQuery(id+"F1.wireOp",EDGE,"E0"),sQuery(id+"F1.wireOp",EDGE,"E3"),sQuery(id+"F1.wireOp",EDGE,"E5"),sQuery(id+"F1.wireOp",EDGE,"E8.MirrorCS")])]}),"instanceName":"68"});
            var Q69;
            Q69=makeQuery(id+"F7.opPattern","COPY",BODY,{"derivedFrom":makeQuery(id+"F3.opExtrude","SWEPT_BODY",BODY,{"disambiguationData":[OSD([sQuery(id+"F1.wireOp",EDGE,"E0"),sQuery(id+"F1.wireOp",EDGE,"E3"),sQuery(id+"F1.wireOp",EDGE,"E5"),sQuery(id+"F1.wireOp",EDGE,"E8.MirrorCS")])]}),"instanceName":"69"});
            var Q70;
            Q70=makeQuery(id+"F7.opPattern","COPY",BODY,{"derivedFrom":makeQuery(id+"F3.opExtrude","SWEPT_BODY",BODY,{"disambiguationData":[OSD([sQuery(id+"F1.wireOp",EDGE,"E0"),sQuery(id+"F1.wireOp",EDGE,"E3"),sQuery(id+"F1.wireOp",EDGE,"E5"),sQuery(id+"F1.wireOp",EDGE,"E8.MirrorCS")])]}),"instanceName":"70"});
            var Q71;
            Q71=makeQuery(id+"F7.opPattern","COPY",BODY,{"derivedFrom":makeQuery(id+"F3.opExtrude","SWEPT_BODY",BODY,{"disambiguationData":[OSD([sQuery(id+"F1.wireOp",EDGE,"E0"),sQuery(id+"F1.wireOp",EDGE,"E3"),sQuery(id+"F1.wireOp",EDGE,"E5"),sQuery(id+"F1.wireOp",EDGE,"E8.MirrorCS")])]}),"instanceName":"71"});
            var Q72;
            Q72=makeQuery(id+"F7.opPattern","COPY",BODY,{"derivedFrom":makeQuery(id+"F3.opExtrude","SWEPT_BODY",BODY,{"disambiguationData":[OSD([sQuery(id+"F1.wireOp",EDGE,"E0"),sQuery(id+"F1.wireOp",EDGE,"E3"),sQuery(id+"F1.wireOp",EDGE,"E5"),sQuery(id+"F1.wireOp",EDGE,"E8.MirrorCS")])]}),"instanceName":"72"});
            var Q73;
            Q73=makeQuery(id+"F7.opPattern","COPY",BODY,{"derivedFrom":makeQuery(id+"F3.opExtrude","SWEPT_BODY",BODY,{"disambiguationData":[OSD([sQuery(id+"F1.wireOp",EDGE,"E0"),sQuery(id+"F1.wireOp",EDGE,"E3"),sQuery(id+"F1.wireOp",EDGE,"E5"),sQuery(id+"F1.wireOp",EDGE,"E8.MirrorCS")])]}),"instanceName":"73"});
            var Q74;
            Q74=makeQuery(id+"F7.opPattern","COPY",BODY,{"derivedFrom":makeQuery(id+"F3.opExtrude","SWEPT_BODY",BODY,{"disambiguationData":[OSD([sQuery(id+"F1.wireOp",EDGE,"E0"),sQuery(id+"F1.wireOp",EDGE,"E3"),sQuery(id+"F1.wireOp",EDGE,"E5"),sQuery(id+"F1.wireOp",EDGE,"E8.MirrorCS")])]}),"instanceName":"74"});
            var Q75;
            Q75=makeQuery(id+"F7.opPattern","COPY",BODY,{"derivedFrom":makeQuery(id+"F3.opExtrude","SWEPT_BODY",BODY,{"disambiguationData":[OSD([sQuery(id+"F1.wireOp",EDGE,"E0"),sQuery(id+"F1.wireOp",EDGE,"E3"),sQuery(id+"F1.wireOp",EDGE,"E5"),sQuery(id+"F1.wireOp",EDGE,"E8.MirrorCS")])]}),"instanceName":"75"});
            var Q76;
            Q76=makeQuery(id+"F7.opPattern","COPY",BODY,{"derivedFrom":makeQuery(id+"F3.opExtrude","SWEPT_BODY",BODY,{"disambiguationData":[OSD([sQuery(id+"F1.wireOp",EDGE,"E0"),sQuery(id+"F1.wireOp",EDGE,"E3"),sQuery(id+"F1.wireOp",EDGE,"E5"),sQuery(id+"F1.wireOp",EDGE,"E8.MirrorCS")])]}),"instanceName":"76"});
            var Q77;
            Q77=makeQuery(id+"F7.opPattern","COPY",BODY,{"derivedFrom":makeQuery(id+"F3.opExtrude","SWEPT_BODY",BODY,{"disambiguationData":[OSD([sQuery(id+"F1.wireOp",EDGE,"E0"),sQuery(id+"F1.wireOp",EDGE,"E3"),sQuery(id+"F1.wireOp",EDGE,"E5"),sQuery(id+"F1.wireOp",EDGE,"E8.MirrorCS")])]}),"instanceName":"77"});
            var Q78;
            Q78=makeQuery(id+"F7.opPattern","COPY",BODY,{"derivedFrom":makeQuery(id+"F3.opExtrude","SWEPT_BODY",BODY,{"disambiguationData":[OSD([sQuery(id+"F1.wireOp",EDGE,"E0"),sQuery(id+"F1.wireOp",EDGE,"E3"),sQuery(id+"F1.wireOp",EDGE,"E5"),sQuery(id+"F1.wireOp",EDGE,"E8.MirrorCS")])]}),"instanceName":"78"});
            var Q79;
            Q79=makeQuery(id+"F7.opPattern","COPY",BODY,{"derivedFrom":makeQuery(id+"F3.opExtrude","SWEPT_BODY",BODY,{"disambiguationData":[OSD([sQuery(id+"F1.wireOp",EDGE,"E0"),sQuery(id+"F1.wireOp",EDGE,"E3"),sQuery(id+"F1.wireOp",EDGE,"E5"),sQuery(id+"F1.wireOp",EDGE,"E8.MirrorCS")])]}),"instanceName":"79"});
            var Q80;
            Q80=makeQuery(id+"F7.opPattern","COPY",BODY,{"derivedFrom":makeQuery(id+"F3.opExtrude","SWEPT_BODY",BODY,{"disambiguationData":[OSD([sQuery(id+"F1.wireOp",EDGE,"E0"),sQuery(id+"F1.wireOp",EDGE,"E3"),sQuery(id+"F1.wireOp",EDGE,"E5"),sQuery(id+"F1.wireOp",EDGE,"E8.MirrorCS")])]}),"instanceName":"80"});
            var Q81;
            Q81=makeQuery(id+"F7.opPattern","COPY",BODY,{"derivedFrom":makeQuery(id+"F3.opExtrude","SWEPT_BODY",BODY,{"disambiguationData":[OSD([sQuery(id+"F1.wireOp",EDGE,"E0"),sQuery(id+"F1.wireOp",EDGE,"E3"),sQuery(id+"F1.wireOp",EDGE,"E5"),sQuery(id+"F1.wireOp",EDGE,"E8.MirrorCS")])]}),"instanceName":"81"});
            var Q82;
            Q82=makeQuery(id+"F7.opPattern","COPY",BODY,{"derivedFrom":makeQuery(id+"F3.opExtrude","SWEPT_BODY",BODY,{"disambiguationData":[OSD([sQuery(id+"F1.wireOp",EDGE,"E0"),sQuery(id+"F1.wireOp",EDGE,"E3"),sQuery(id+"F1.wireOp",EDGE,"E5"),sQuery(id+"F1.wireOp",EDGE,"E8.MirrorCS")])]}),"instanceName":"82"});
            var Q83;
            Q83=makeQuery(id+"F7.opPattern","COPY",BODY,{"derivedFrom":makeQuery(id+"F3.opExtrude","SWEPT_BODY",BODY,{"disambiguationData":[OSD([sQuery(id+"F1.wireOp",EDGE,"E0"),sQuery(id+"F1.wireOp",EDGE,"E3"),sQuery(id+"F1.wireOp",EDGE,"E5"),sQuery(id+"F1.wireOp",EDGE,"E8.MirrorCS")])]}),"instanceName":"83"});
            var Q84;
            Q84=makeQuery(id+"F7.opPattern","COPY",BODY,{"derivedFrom":makeQuery(id+"F3.opExtrude","SWEPT_BODY",BODY,{"disambiguationData":[OSD([sQuery(id+"F1.wireOp",EDGE,"E0"),sQuery(id+"F1.wireOp",EDGE,"E3"),sQuery(id+"F1.wireOp",EDGE,"E5"),sQuery(id+"F1.wireOp",EDGE,"E8.MirrorCS")])]}),"instanceName":"84"});
            var Q85;
            Q85=makeQuery(id+"F7.opPattern","COPY",BODY,{"derivedFrom":makeQuery(id+"F3.opExtrude","SWEPT_BODY",BODY,{"disambiguationData":[OSD([sQuery(id+"F1.wireOp",EDGE,"E0"),sQuery(id+"F1.wireOp",EDGE,"E3"),sQuery(id+"F1.wireOp",EDGE,"E5"),sQuery(id+"F1.wireOp",EDGE,"E8.MirrorCS")])]}),"instanceName":"85"});
            var Q86;
            Q86=makeQuery(id+"F7.opPattern","COPY",BODY,{"derivedFrom":makeQuery(id+"F3.opExtrude","SWEPT_BODY",BODY,{"disambiguationData":[OSD([sQuery(id+"F1.wireOp",EDGE,"E0"),sQuery(id+"F1.wireOp",EDGE,"E3"),sQuery(id+"F1.wireOp",EDGE,"E5"),sQuery(id+"F1.wireOp",EDGE,"E8.MirrorCS")])]}),"instanceName":"86"});
            var Q87;
            Q87=makeQuery(id+"F7.opPattern","COPY",BODY,{"derivedFrom":makeQuery(id+"F3.opExtrude","SWEPT_BODY",BODY,{"disambiguationData":[OSD([sQuery(id+"F1.wireOp",EDGE,"E0"),sQuery(id+"F1.wireOp",EDGE,"E3"),sQuery(id+"F1.wireOp",EDGE,"E5"),sQuery(id+"F1.wireOp",EDGE,"E8.MirrorCS")])]}),"instanceName":"87"});
            var Q88;
            Q88=makeQuery(id+"F7.opPattern","COPY",BODY,{"derivedFrom":makeQuery(id+"F3.opExtrude","SWEPT_BODY",BODY,{"disambiguationData":[OSD([sQuery(id+"F1.wireOp",EDGE,"E0"),sQuery(id+"F1.wireOp",EDGE,"E3"),sQuery(id+"F1.wireOp",EDGE,"E5"),sQuery(id+"F1.wireOp",EDGE,"E8.MirrorCS")])]}),"instanceName":"88"});
            var Q89;
            Q89=makeQuery(id+"F7.opPattern","COPY",BODY,{"derivedFrom":makeQuery(id+"F3.opExtrude","SWEPT_BODY",BODY,{"disambiguationData":[OSD([sQuery(id+"F1.wireOp",EDGE,"E0"),sQuery(id+"F1.wireOp",EDGE,"E3"),sQuery(id+"F1.wireOp",EDGE,"E5"),sQuery(id+"F1.wireOp",EDGE,"E8.MirrorCS")])]}),"instanceName":"89"});
            var Q90;
            Q90=makeQuery(id+"F6.opExtrude","SWEPT_BODY",BODY,{"disambiguationData":[OSD([sQuery(id+"F2.wireOp",EDGE,"E10")])]});
            booleanBodies(context, id + "F8", {"operationType" : BooleanOperationType.SUBTRACTION, "tools" : qUnion([Q0, Q1, Q2, Q3, Q4, Q5, Q6, Q7, Q8, Q9, Q10, Q11, Q12, Q13, Q14, Q15, Q16, Q17, Q18, Q19, Q20, Q21, Q22, Q23, Q24, Q25, Q26, Q27, Q28, Q29, Q30, Q31, Q32, Q33, Q34, Q35, Q36, Q37, Q38, Q39, Q40, Q41, Q42, Q43, Q44, Q45, Q46, Q47, Q48, Q49, Q50, Q51, Q52, Q53, Q54, Q55, Q56, Q57, Q58, Q59, Q60, Q61, Q62, Q63, Q64, Q65, Q66, Q67, Q68, Q69, Q70, Q71, Q72, Q73, Q74, Q75, Q76, Q77, Q78, Q79, Q80, Q81, Q82, Q83, Q84, Q85, Q86, Q87, Q88, Q89]), "targets" : qUnion([Q90])});
        }
        {
            var Q0;
            Q0=makeQuery(id+"F6.opExtrude","CAP_FACE",FACE,{"disambiguationData":[OSD([sQuery(id+"F2.wireOp",EDGE,"E10")])],"isStart":true});
            var sketch = newSketch(context, id + "F9", { "sketchPlane" : qUnion([Q0])});
            skCircle(sketch, "E12", {"center": v(0, 0) * mm, "radius": 3.17 * mm});
            skCircle(sketch, "E13", {"center": v(0, 0) * mm, "radius": 12.5 * mm});
            skCircle(sketch, "E14", {"center": v(0, 0) * mm, "radius": 60 * mm});
            skLineSegment(sketch, "E15", {"start": v(0, 0) * mm, "end": v(0, 60) * mm, "construction": true});
            skLineSegment(sketch, "E16.0", {"start": v(5, 0) * mm, "end": v(5, 59.79) * mm});
            skLineSegment(sketch, "E17", {"start": v(0, 0) * mm, "end": v(60.62, -35) * mm, "construction": true});
            skLineSegment(sketch, "E18.0", {"start": v(2.5, 4.33) * mm, "end": v(62.96, -30.58) * mm});
            skCircle(sketch, "E19", {"center": v(0, 0) * mm, "radius": 70 * mm});
            skSolve(sketch);
        }
        {
            var Q0;
            Q0=makeQuery(id+"F9.imprint","IMPRINT",FACE,{"disambiguationData":[TD([[makeQuery(id+"F9.imprint","IMPRINT",EDGE,{"derivedFrom":sQuery(id+"F9.wireOp",EDGE,"E12")}),1.0]])]});
            extrude(context, id + "F10", {"entities" : qUnion([Q0]), "operationType" : NewBodyOperationType.REMOVE, "oppositeDirection" : true, "depth" : 25 * mm});
        }
    });
